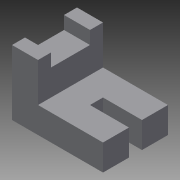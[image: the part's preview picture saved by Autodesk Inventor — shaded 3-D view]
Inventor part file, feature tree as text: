
AUTODESK INVENTOR PART (.ipt)
format: ipt  version: 2015 (Build 190159000, 159)  size: 91,136 bytes
history: native  units: in
note: dims shown in document units (in); Inventor stores cm internally (conversion verified against a paired STEP export)
features: extrude x3, sketch x3
ambient origin geometry x8: Origin, YZ Plane, XZ Plane, XY Plane, X Axis, Y Axis, Z Axis, Center Point
bodies: Solid1 (feature_tree)
feature tree (6):
  extrude  "Extrusion1"  Depth=0.75in
  extrude  "Extrusion2"  Depth=0.75in TaperAngle=0.0deg
  extrude  "Extrusion3"  Depth=0.75in
  sketch  "Sketch1"  dims[d0=1.75in d3=0.75in]
  sketch  "Sketch3"  dims[d4=1.25in d5=0.0in d10=0.75in d11=0.0in]
  sketch  "Sketch4"  dims[d13=0.5in d14=0.75in d15=0.25in d16=0.0in]
